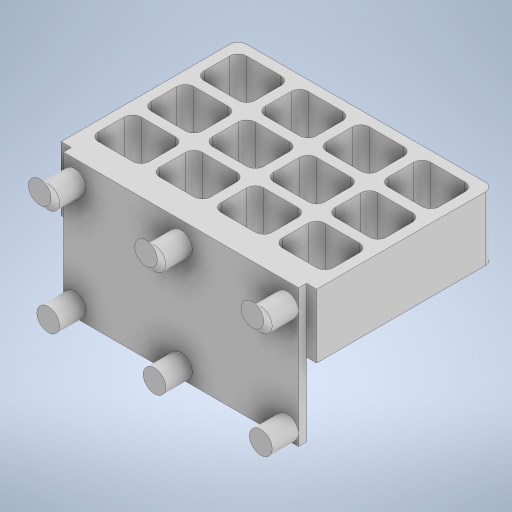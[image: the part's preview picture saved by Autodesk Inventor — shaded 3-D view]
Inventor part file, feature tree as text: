
AUTODESK INVENTOR PART (.ipt)
format: ipt  version: 2024 (Build 280153000, 153)  size: 419,840 bytes
history: native  units: mm
features: sketch x5, extrude x4, other x3, pattern_linear x3, fillet x2, chamfer x2, loft x1
ambient origin geometry x8: Origin, YZ Plane, XZ Plane, XY Plane, X Axis, Y Axis, Z Axis, Center Point
bodies: Body1 (feature_tree)
feature tree (20):
  other  "Твердое тело1"
  extrude  "Выдавливание1"  Depth=1.85mm TaperAngle=0.0deg
  extrude  "Выдавливание2"  Depth=55.2mm
  pattern_linear  "Прямоуг.массив1"  Spacing1=32.25mm  [1 undecoded]
  extrude  "Выдавливание3"  Depth=5.3mm
  extrude  "Выдавливание4"  Depth=6.2mm TaperAngle=0.0deg
  fillet  "Сопряжение1"  Radius=20.0mm
  pattern_linear  "Прямоуг.массив2"  Spacing1=24.95mm  [1 undecoded]
  fillet  "Сопряжение2"  Radius=15.0mm
  other  "РабПлоскость1"
  loft  "Лофт1"
  pattern_linear  "Прямоуг.массив3"  Spacing1=12.0mm  [1 undecoded]
  chamfer  "Фаска1"  Distance=13.0mm
  chamfer  "Фаска2"  [1 undecoded]
  sketch  "Эскиз1"
  sketch  "Эскиз2"
  sketch  "Эскиз3"
  sketch  "Эскиз4"
  sketch  "Эскиз7"
  other  "Ребра1"
note: 4 required parameter values undecoded (feature->parameter linkage not recoverable at this tier; creation-order binding heuristic only, values carry confidence <= 0.55)
